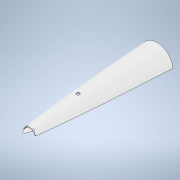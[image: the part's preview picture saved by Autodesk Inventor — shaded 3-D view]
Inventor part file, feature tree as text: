
AUTODESK INVENTOR PART (.ipt)
format: ipt  version: 2020.3 (Build 243373000, 373)  size: 336,896 bytes
history: native  units: mm
features: extrude x3, fillet x3, sketch x2, revolve x2
ambient origin geometry x8: Origin, YZ Plane, XZ Plane, XY Plane, X Axis, Y Axis, Z Axis, Center Point
bodies: Body1 (feature_tree)
feature tree (10):
  sketch  "Sketch3"  dims[d54=25.9mm d55=5.0mm d56=0.9mm d57=2.0mm d58=25.9mm d59=5.0mm d60=0.9mm d61=212.5mm d62=250.0mm d63=25.0mm d64=25.0mm d65=248.2mm d66=25.0mm d67=2.0mm d68=212.5mm d69=5.0mm d70=8.0mm d71=212.5mm d72=15.232132mm d73=360.0deg]
  revolve  "Revolution5"  Angle=360.0deg
  extrude  "Extrusion5"  Depth=3.0mm
  extrude  "Extrusion7"  Depth=2.0mm
  revolve  "Revolution6"  [1 undecoded]
  extrude  "Extrusion8"  Depth=3.0mm
  fillet  "Fillet1"  Radius=256.25mm
  fillet  "Fillet2"  [1 undecoded]
  fillet  "Fillet3"  Radius=5.0mm
  sketch  "Sketch5"  dims[d74=60.0mm d75=0.0mm d78=3.0mm d79=2.0mm d80=14.0mm d81=0.0mm d82=3.0mm d83=256.25mm d84=360.0deg d85=5.0mm d86=25.0mm d87=0.0mm d88=2.0mm d89=2.0mm d90=2.0mm d7=0.872665mm d8=0.872665mm d21=0.5mm d22=0.872665mm d23=0.5mm d24=0.872665mm]
note: 2 required parameter values undecoded (feature->parameter linkage not recoverable at this tier; creation-order binding heuristic only, values carry confidence <= 0.55)